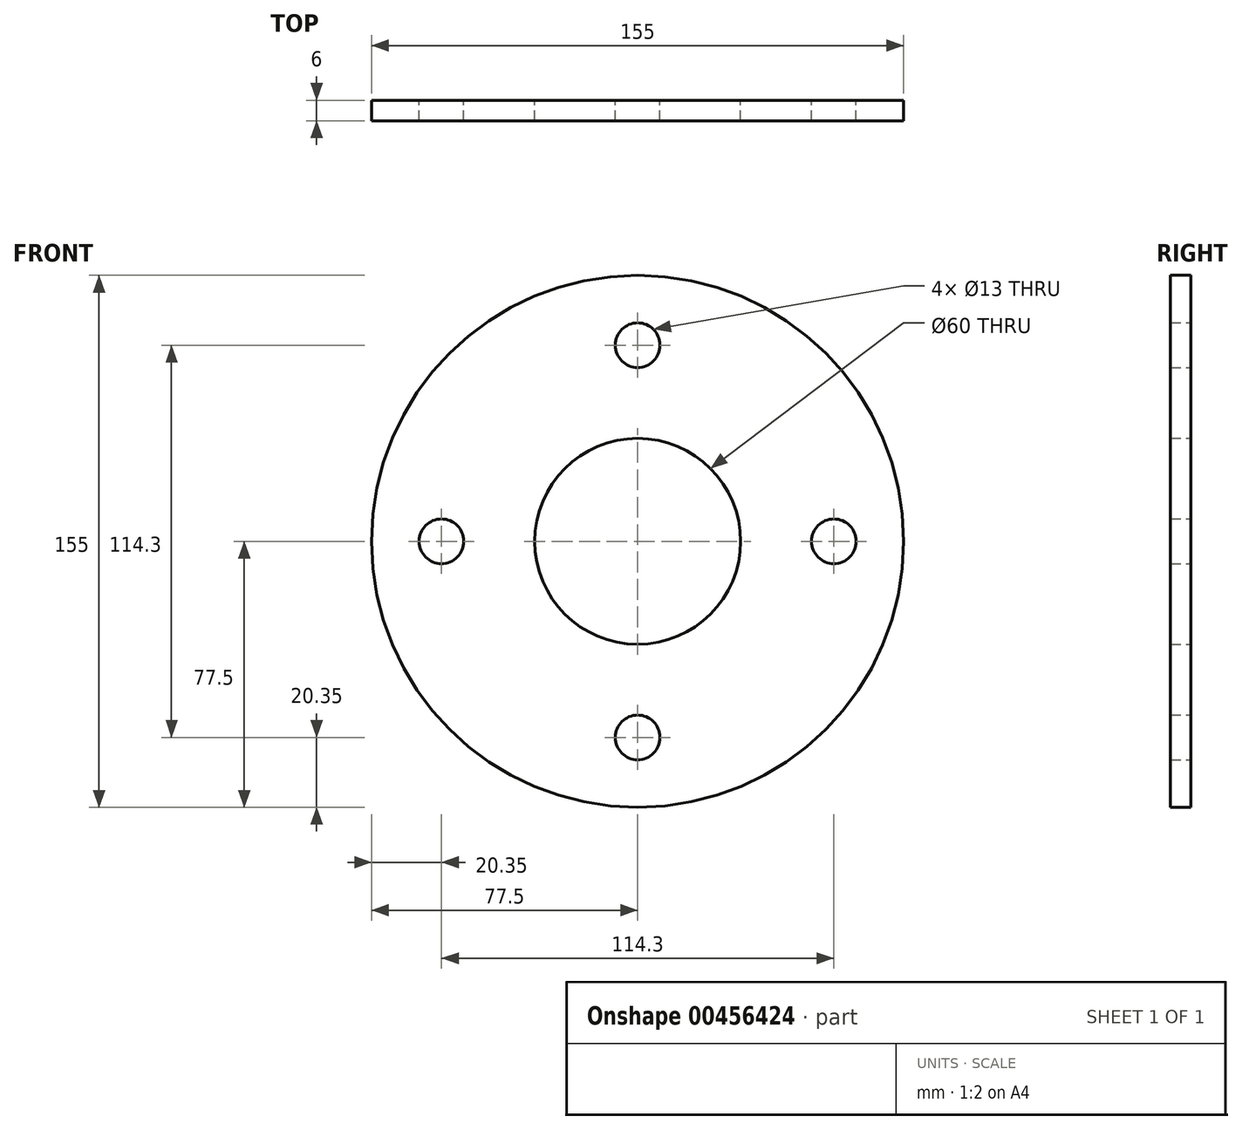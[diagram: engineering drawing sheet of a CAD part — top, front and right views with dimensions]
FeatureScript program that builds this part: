
annotation { "Feature Type Name" : "Feature", "Feature Type Description" : "" }
export const myFeature = defineFeature(function(context is Context, id is Id, definition is map)
    precondition{}
    {
        {
            var Q0;
            Q0=qCreatedBy(makeId("Front.planeOp"),FACE);
            var sketch = newSketch(context, id + "F0", { "sketchPlane" : qUnion([Q0])});
            skCircle(sketch, "E0", {"center": v(0, 0) * mm, "radius": 30 * mm});
            skCircle(sketch, "E1", {"center": v(0, 0) * mm, "radius": 77.5 * mm});
            skCircle(sketch, "E2", {"center": v(0, 57.15) * mm, "radius": 6.5 * mm});
            skCircle(sketch, "E3", {"center": v(57.15, 0) * mm, "radius": 6.5 * mm});
            skCircle(sketch, "E4", {"center": v(0, -57.15) * mm, "radius": 6.5 * mm});
            skCircle(sketch, "E5", {"center": v(-57.15, 0) * mm, "radius": 6.5 * mm});
            skSolve(sketch);
        }
        {
            var Q0;
            Q0=makeQuery(id+"F0.imprint","IMPRINT",FACE,{"disambiguationData":[TD([[makeQuery(id+"F0.imprint","IMPRINT",EDGE,{"derivedFrom":sQuery(id+"F0.wireOp",EDGE,"E0")}),-1.0]])]});
            extrude(context, id + "F1", {"entities" : qUnion([Q0]), "depth" : 6 * mm});
        }
    });
